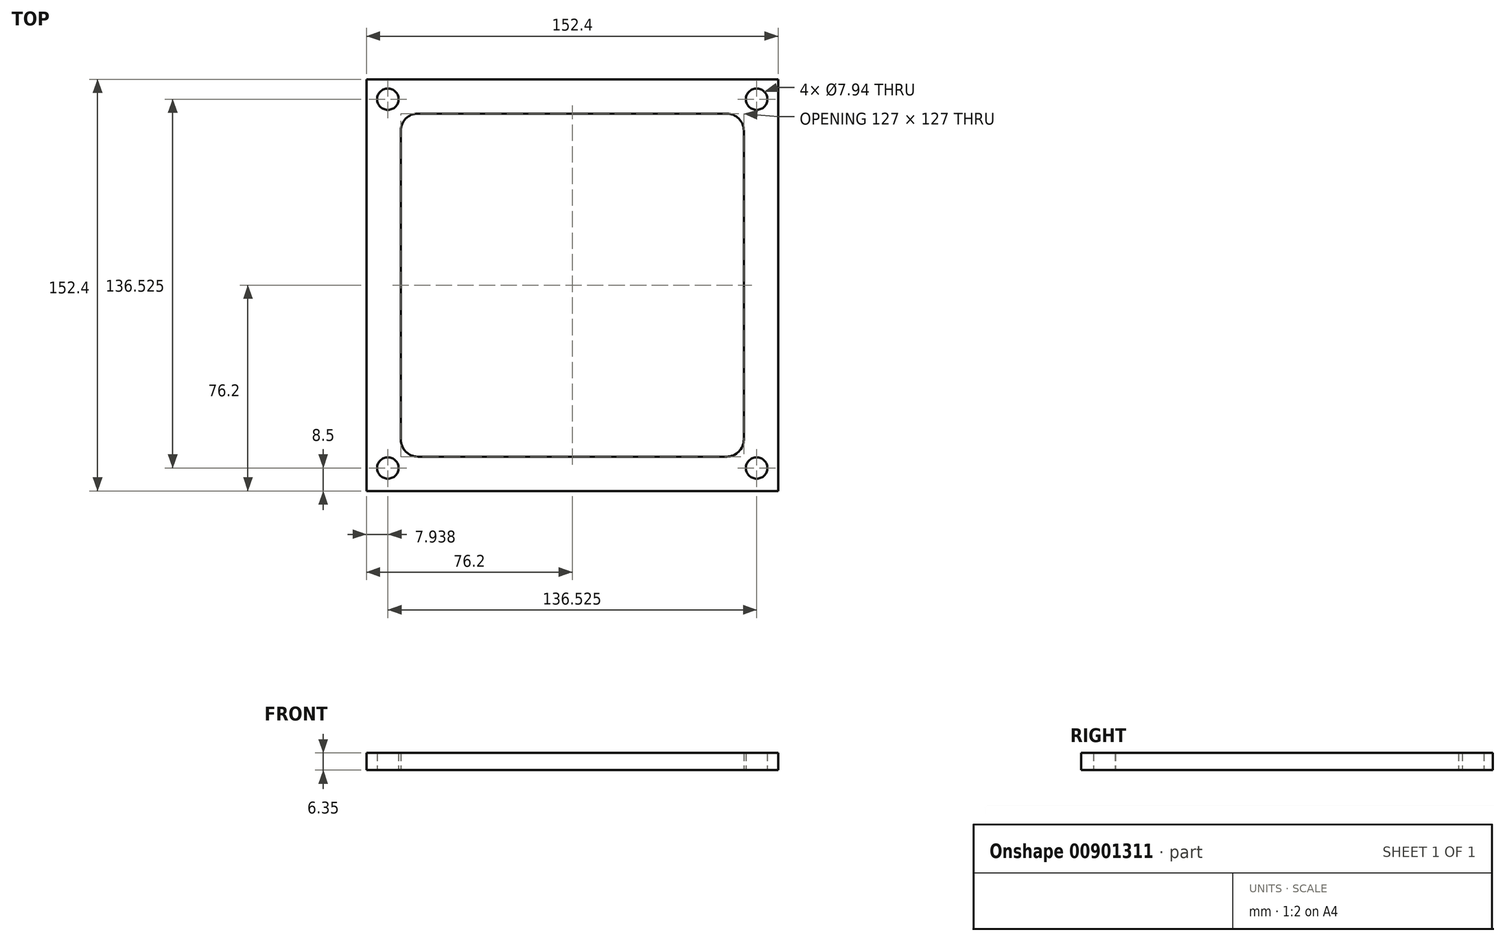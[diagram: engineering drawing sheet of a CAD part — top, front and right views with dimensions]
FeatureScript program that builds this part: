
annotation { "Feature Type Name" : "Feature", "Feature Type Description" : "" }
export const myFeature = defineFeature(function(context is Context, id is Id, definition is map)
    precondition{}
    {
        {
            var Q0;
            Q0=qCreatedBy(makeId("Top.planeOp"),FACE);
            var sketch = newSketch(context, id + "F0", { "sketchPlane" : qUnion([Q0])});
            skLineSegment(sketch, "E0.bottom", {"start": v(0, 0) * mm, "end": v(152.4, 0) * mm});
            skLineSegment(sketch, "E0.top", {"start": v(0, 152.4) * mm, "end": v(152.4, 152.4) * mm});
            skLineSegment(sketch, "E0.left", {"start": v(0, 0) * mm, "end": v(0, 152.4) * mm});
            skLineSegment(sketch, "E0.right", {"start": v(152.4, 0) * mm, "end": v(152.4, 152.4) * mm});
            skLineSegment(sketch, "E1.bottom", {"start": v(19.05, 12.7) * mm, "end": v(133.35, 12.7) * mm});
            skLineSegment(sketch, "E1.top", {"start": v(19.05, 139.7) * mm, "end": v(133.35, 139.7) * mm});
            skLineSegment(sketch, "E1.left", {"start": v(12.7, 19.05) * mm, "end": v(12.7, 133.35) * mm});
            skLineSegment(sketch, "E1.right", {"start": v(139.7, 19.05) * mm, "end": v(139.7, 133.35) * mm});
            skCircle(sketch, "E2", {"center": v(7.94, 8.5) * mm, "radius": 3.97 * mm});
            skPoint(sketch, "E3.visualSharp", {"position": v(12.7, 12.7) * mm});
            skArc(sketch, "E3.filletArc", {"start": v(12.7, 19.05) * mm, "mid": v(14.56, 14.56) * mm, "end": v(19.05, 12.7) * mm});
            skPoint(sketch, "E4.visualSharp", {"position": v(139.7, 12.7) * mm});
            skArc(sketch, "E4.filletArc", {"start": v(133.35, 12.7) * mm, "mid": v(137.84, 14.56) * mm, "end": v(139.7, 19.05) * mm});
            skPoint(sketch, "E5.visualSharp", {"position": v(139.7, 139.7) * mm});
            skArc(sketch, "E5.filletArc", {"start": v(139.7, 133.35) * mm, "mid": v(137.84, 137.84) * mm, "end": v(133.35, 139.7) * mm});
            skCircle(sketch, "E6.0.1.0", {"center": v(7.94, 145.02) * mm, "radius": 3.97 * mm});
            skCircle(sketch, "E6.1.0.0", {"center": v(144.46, 8.5) * mm, "radius": 3.97 * mm});
            skCircle(sketch, "E6.1.1.0", {"center": v(144.46, 145.02) * mm, "radius": 3.97 * mm});
            skLineSegment(sketch, "E6.direction1", {"start": v(7.94, 8.5) * mm, "end": v(144.46, 8.5) * mm, "construction": true});
            skLineSegment(sketch, "E6.direction2", {"start": v(7.94, 8.5) * mm, "end": v(7.94, 145.02) * mm, "construction": true});
            skPoint(sketch, "E7.visualSharp", {"position": v(12.7, 139.7) * mm});
            skArc(sketch, "E7.filletArc", {"start": v(19.05, 139.7) * mm, "mid": v(14.56, 137.84) * mm, "end": v(12.7, 133.35) * mm});
            skSolve(sketch);
        }
        {
            var Q0;
            Q0=makeQuery(id+"F0.imprint","IMPRINT",FACE,{"disambiguationData":[TD([[makeQuery(id+"F0.imprint","IMPRINT",EDGE,{"derivedFrom":sQuery(id+"F0.wireOp",EDGE,"E0.bottom")}),1.0]])]});
            extrude(context, id + "F1", {"entities" : qUnion([Q0]), "depth" : 6.35 * mm, "offsetDistance" : 25.4 * mm});
        }
    });
